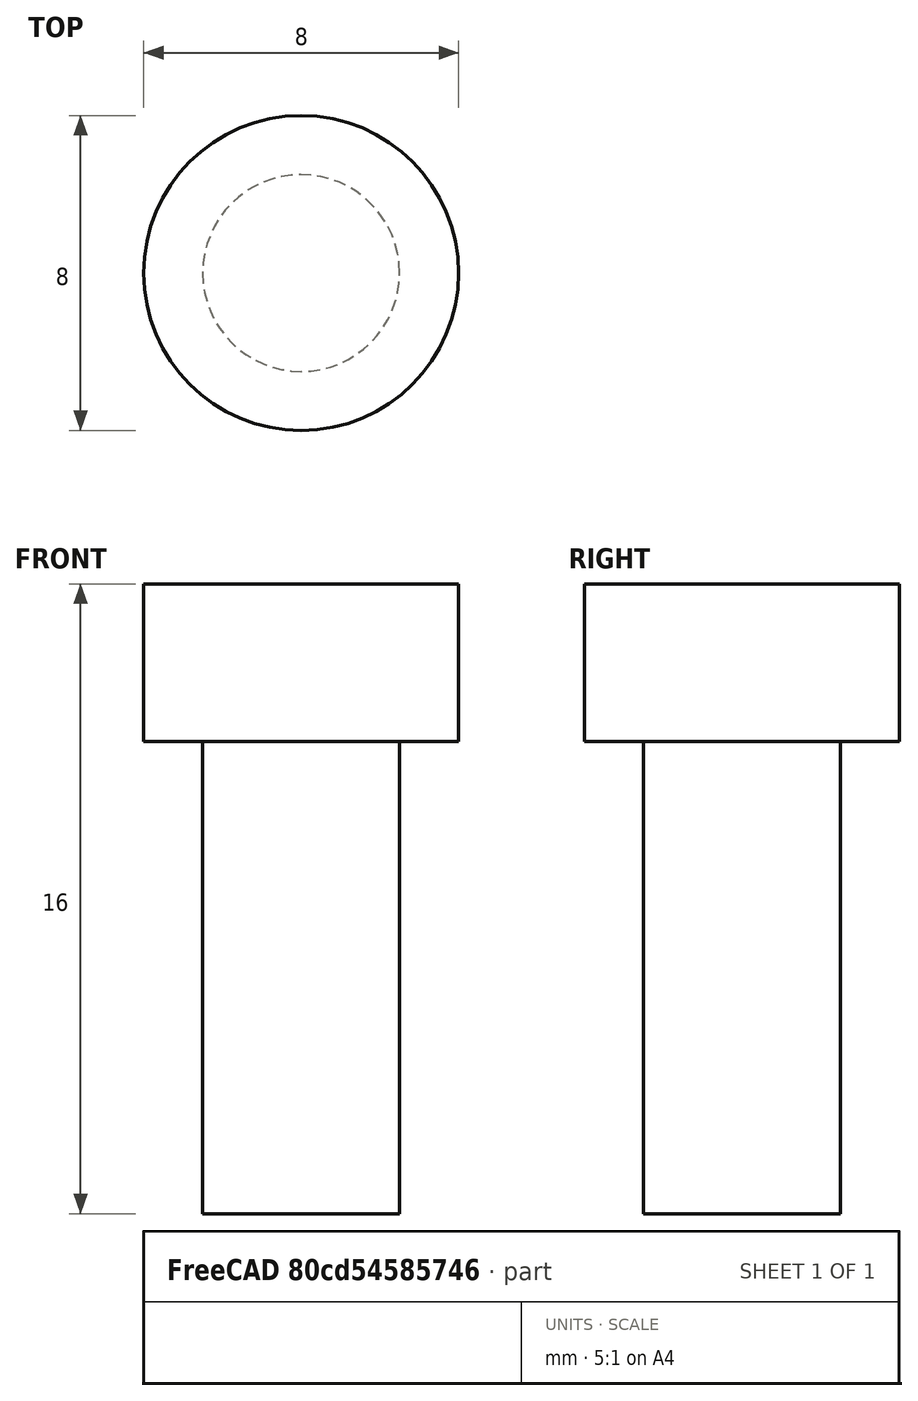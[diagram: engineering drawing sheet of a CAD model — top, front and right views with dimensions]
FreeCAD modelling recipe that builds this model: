
FCSTD DOCUMENT  (FreeCAD 0.18R14555 (Git shallow))
Label: m5-12
License: All rights reserved
LicenseURL: http://en.wikipedia.org/wiki/All_rights_reserved
objects: Sketcher::SketchObject×1, PartDesign::Revolution×1, PartDesign::Body×1
note: 4 computed .brp shape members not serialized (recipe doc carries the construction recipe); baked Part::Feature solids carry a one-line shape summary decoded from their .brp

FEATURE [Sketcher::SketchObject] Sketch
  MapMode = 5
  Placement = pos=(0,0,0) rot=(1,0,0;1.5708rad)
  Support = -> [XZ_Plane]
  sketch-geometry (6):
    g0: LineSegment StartX=0 StartY=0 StartZ=0 EndX=2.5 EndY=0 EndZ=0
    g1: LineSegment StartX=2.5 StartY=0 StartZ=0 EndX=2.5 EndY=12 EndZ=0
    g2: LineSegment StartX=2.5 StartY=12 StartZ=0 EndX=4 EndY=12 EndZ=0
    g3: LineSegment StartX=4 StartY=12 StartZ=0 EndX=4 EndY=16 EndZ=0
    g4: LineSegment StartX=4 StartY=16 StartZ=0 EndX=0 EndY=16 EndZ=0
    g5: LineSegment StartX=0 StartY=16 StartZ=0 EndX=0 EndY=0 EndZ=0
  constraints (17):
    c: Horizontal(g0)
    c: Coincident(g0,g1)
    c: Vertical(g1)
    c: Coincident(g1,g2)
    c: Horizontal(g2)
    c: Coincident(g2,g3)
    c: Vertical(g3)
    c: Coincident(g3,g4)
    c: Horizontal(g4)
    c: Coincident(g4,g5)
    c: Coincident(g5,g0)
    c: Vertical(g5)
    c: Coincident(g0,g-1)
    c: DistanceX(g0,g0) = 2.5
    c: DistanceY(g1,g1) = 12
    c: DistanceY(g3,g3) = 4
    c: DistanceX(g4,g4) = 4
FEATURE [PartDesign::Revolution] Revolution
  Angle = 360
  Axis = (0,2e-16,1)
  Base = (0,0,0)
  Placement = pos=(0,0,0) rot=(1,0,0;1.5708rad)
  Profile = -> Sketch
  ReferenceAxis = -> Sketch [V_Axis]
  Reversed = true
FEATURE [PartDesign::Body] Body
  Group = -> [Sketch,Revolution]
  Origin = -> Origin
  Tip = -> Revolution
